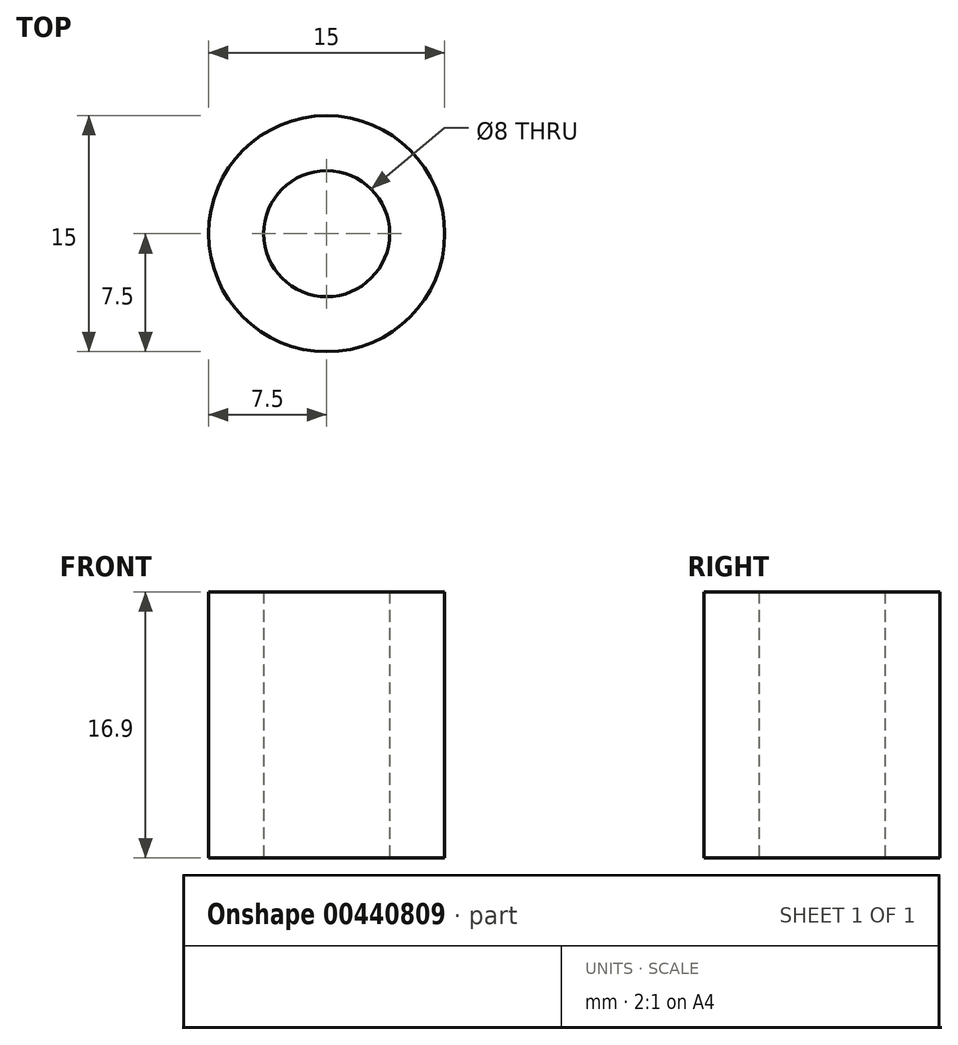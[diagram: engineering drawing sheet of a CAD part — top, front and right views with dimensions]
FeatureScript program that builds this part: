
annotation { "Feature Type Name" : "Feature", "Feature Type Description" : "" }
export const myFeature = defineFeature(function(context is Context, id is Id, definition is map)
    precondition{}
    {
        {
            var Q0;
            Q0=qCreatedBy(makeId("Top.planeOp"),FACE);
            var sketch = newSketch(context, id + "F0", { "sketchPlane" : qUnion([Q0])});
            skCircle(sketch, "E0", {"center": v(0, 0) * mm, "radius": 7.5 * mm});
            skCircle(sketch, "E1", {"center": v(0, 0) * mm, "radius": 4 * mm});
            skSolve(sketch);
        }
        {
            var Q0;
            Q0 = qSketchRegion(id + "F0", true);
            extrude(context, id + "F1", {"entities" : qUnion([Q0]), "depth" : 16.9 * mm});
        }
    });
